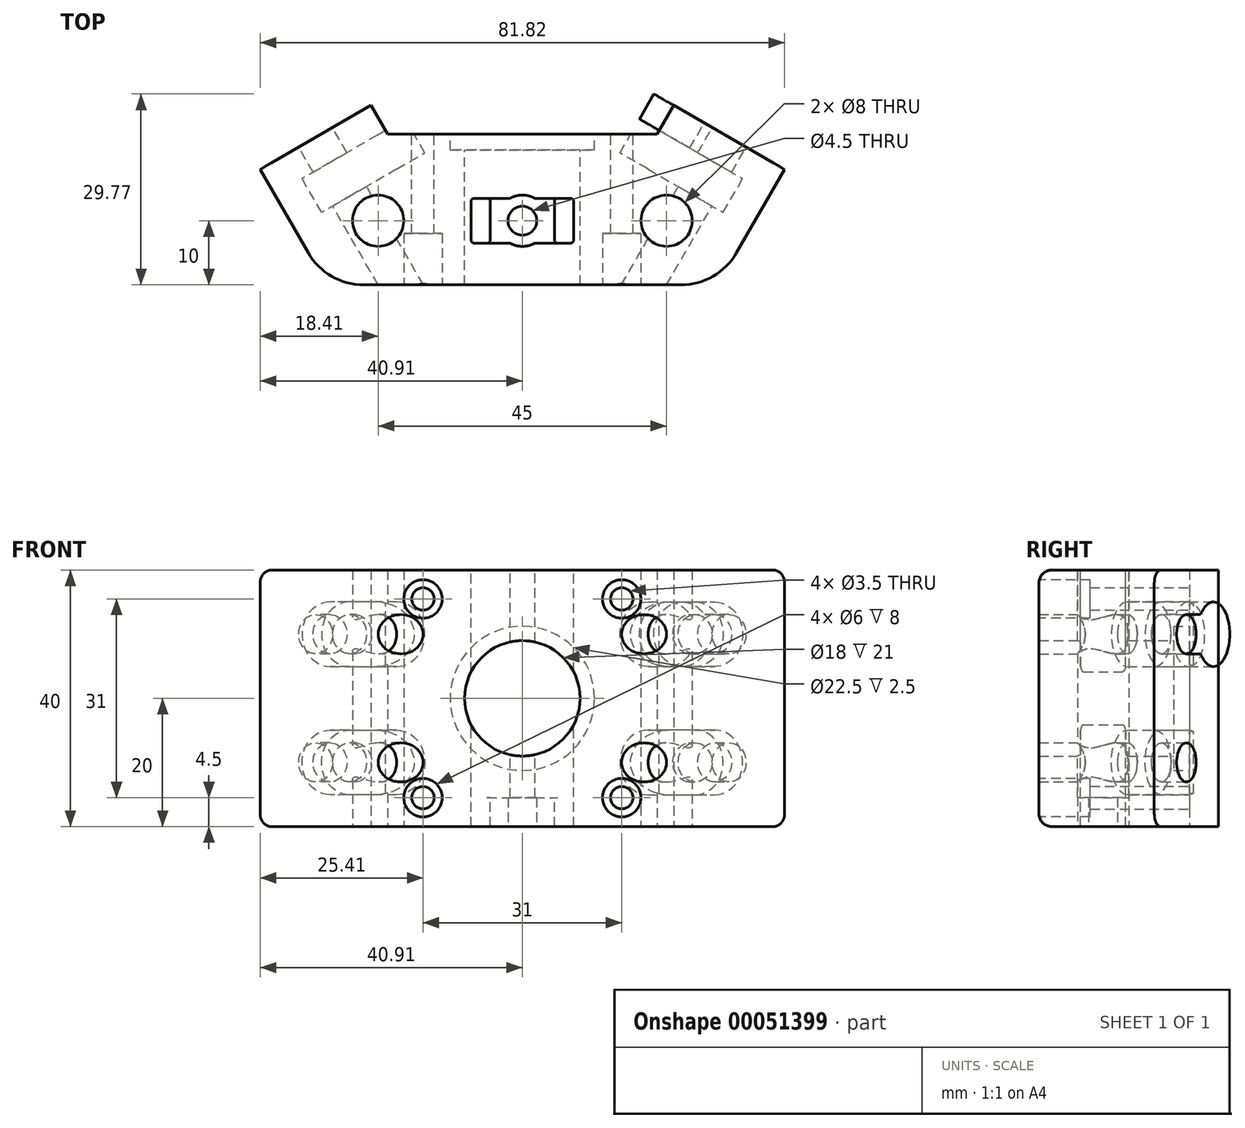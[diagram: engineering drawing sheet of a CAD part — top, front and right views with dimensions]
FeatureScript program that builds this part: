
annotation { "Feature Type Name" : "Feature", "Feature Type Description" : "" }
export const myFeature = defineFeature(function(context is Context, id is Id, definition is map)
    precondition{}
    {
        {
            var Q0;
            Q0=qCreatedBy(makeId("Top.planeOp"),FACE);
            var sketch = newSketch(context, id + "F0", { "sketchPlane" : qUnion([Q0])});
            skLineSegment(sketch, "E0", {"start": v(-22.5, 0) * mm, "end": v(22.5, 0) * mm, "construction": true});
            skCircle(sketch, "E1", {"center": v(22.5, 0) * mm, "radius": 4 * mm});
            skCircle(sketch, "E2", {"center": v(-22.5, 0) * mm, "radius": 4 * mm});
            skLineSegment(sketch, "E3", {"start": v(0, 0) * mm, "end": v(0, 13.5) * mm, "construction": true});
            skLineSegment(sketch, "E4", {"start": v(-21, 13.5) * mm, "end": v(21, 13.5) * mm});
            skLineSegment(sketch, "E5", {"start": v(23.6, 18) * mm, "end": v(40.91, 8) * mm});
            skLineSegment(sketch, "E6", {"start": v(40.91, 8) * mm, "end": v(33.41, -5) * mm});
            skLineSegment(sketch, "E7", {"start": v(24.75, -10) * mm, "end": v(-24.75, -10) * mm});
            skLineSegment(sketch, "E8", {"start": v(0, -10) * mm, "end": v(0, 0) * mm, "construction": true});
            skLineSegment(sketch, "E9", {"start": v(23.6, 18) * mm, "end": v(21, 13.5) * mm});
            skLineSegment(sketch, "E10", {"start": v(22.5, 0) * mm, "end": v(30.56, 13.97) * mm, "construction": true});
            skArc(sketch, "E11", {"start": v(33.41, -5) * mm, "mid": v(29.75, -8.66) * mm, "end": v(24.75, -10) * mm});
            skArc(sketch, "E12.MirrorCS", {"start": v(-33.41, -5) * mm, "mid": v(-29.75, -8.66) * mm, "end": v(-24.75, -10) * mm});
            skLineSegment(sketch, "E13.MirrorCS", {"start": v(-40.91, 8) * mm, "end": v(-33.41, -5) * mm});
            skLineSegment(sketch, "E14.MirrorCS", {"start": v(-23.6, 18) * mm, "end": v(-21, 13.5) * mm});
            skLineSegment(sketch, "E15.MirrorCS", {"start": v(-23.6, 18) * mm, "end": v(-40.91, 8) * mm});
            skSolve(sketch);
        }
        {
            var Q0;
            Q0 = qSketchRegion(id + "F0", true);
            extrude(context, id + "F1", {"entities" : qUnion([Q0]), "endBound" : BoundingType.SYMMETRIC, "depth" : 40 * mm});
        }
        {
            var Q0;
            Q0=makeQuery(id+"F1.opExtrude","SWEPT_FACE",FACE,{"disambiguationData":[OSD([sQuery(id+"F0.wireOp",EDGE,"E4")])]});
            var sketch = newSketch(context, id + "F2", { "sketchPlane" : qUnion([Q0])});
            skLineSegment(sketch, "E16", {"start": v(0, 20) * mm, "end": v(0, -20) * mm, "construction": true});
            skCircle(sketch, "E17", {"center": v(0, 0) * mm, "radius": 11.25 * mm});
            skSolve(sketch);
        }
        {
            var Q0;
            Q0 = qSketchRegion(id + "F2", true);
            extrude(context, id + "F3", {"entities" : qUnion([Q0]), "operationType" : NewBodyOperationType.REMOVE, "oppositeDirection" : true, "depth" : 2.5 * mm});
        }
        {
            var Q0;
            Q0=makeQuery(id+"F3.boolean.opBoolean","COPY",FACE,{"derivedFrom":makeQuery(id+"F3.opExtrude","CAP_FACE",FACE,{"disambiguationData":[OSD([sQuery(id+"F2.wireOp",EDGE,"E17")])],"isStart":false})});
            var sketch = newSketch(context, id + "F4", { "sketchPlane" : qUnion([Q0])});
            skCircle(sketch, "E18", {"center": v(0, 0) * mm, "radius": 9 * mm});
            skSolve(sketch);
        }
        {
            var Q0;
            Q0 = qSketchRegion(id + "F4", true);
            extrude(context, id + "F5", {"entities" : qUnion([Q0]), "operationType" : NewBodyOperationType.REMOVE, "endBound" : BoundingType.UP_TO_NEXT, "oppositeDirection" : true, "depth" : 25 * mm});
        }
        {
            var Q0;
            Q0=makeQuery(id+"F1.opExtrude","SWEPT_FACE",FACE,{"disambiguationData":[OSD([sQuery(id+"F0.wireOp",EDGE,"E4")])]});
            var sketch = newSketch(context, id + "F6", { "sketchPlane" : qUnion([Q0])});
            skLineSegment(sketch, "E19.rect.bottom", {"start": v(15.5, 15.5) * mm, "end": v(-15.5, 15.5) * mm, "construction": true});
            skLineSegment(sketch, "E19.rect.top", {"start": v(15.5, -15.5) * mm, "end": v(-15.5, -15.5) * mm, "construction": true});
            skLineSegment(sketch, "E19.rect.left", {"start": v(15.5, 15.5) * mm, "end": v(15.5, -15.5) * mm, "construction": true});
            skLineSegment(sketch, "E19.rect.right", {"start": v(-15.5, 15.5) * mm, "end": v(-15.5, -15.5) * mm, "construction": true});
            skPoint(sketch, "E19.rect.middle", {"position": v(0, 0) * mm});
            skSolve(sketch);
        }
        {
            var Q0;
            Q0=sQuery(id+"F6.wireOp",VERTEX,"E19.rect.right.start");
            var Q1;
            Q1=sQuery(id+"F6.wireOp",VERTEX,"E19.rect.left.start");
            var Q2;
            Q2=sQuery(id+"F6.wireOp",VERTEX,"E19.rect.left.end");
            var Q3;
            Q3=sQuery(id+"F6.wireOp",VERTEX,"E19.rect.right.end");
            var Q4;
            Q4=makeQuery(id+"F1.opExtrude","SWEPT_BODY",BODY,{"disambiguationData":[OSD([sQuery(id+"F0.wireOp",EDGE,"E1"),sQuery(id+"F0.wireOp",EDGE,"E2"),sQuery(id+"F0.wireOp",EDGE,"E4"),sQuery(id+"F0.wireOp",EDGE,"E5"),sQuery(id+"F0.wireOp",EDGE,"E6"),sQuery(id+"F0.wireOp",EDGE,"E7"),sQuery(id+"F0.wireOp",EDGE,"E9"),sQuery(id+"F0.wireOp",EDGE,"E11"),sQuery(id+"F0.wireOp",EDGE,"E12.MirrorCS"),sQuery(id+"F0.wireOp",EDGE,"E13.MirrorCS"),sQuery(id+"F0.wireOp",EDGE,"E14.MirrorCS"),sQuery(id+"F0.wireOp",EDGE,"E15.MirrorCS")])]});
            hole(context, id + "F7", {"style" : HoleStyle.SIMPLE, "holeDiameter" : 3.5 * mm, "endStyle" : HoleEndStyle.THROUGH, "locations" : qUnion([Q0, Q1, Q2, Q3]), "scope" : qUnion([Q4])});
        }
        {
            var Q0;
            Q0=makeQuery(id+"F1.opExtrude","SWEPT_FACE",FACE,{"disambiguationData":[OSD([sQuery(id+"F0.wireOp",EDGE,"E5")])]});
            var sketch = newSketch(context, id + "F8", { "sketchPlane" : qUnion([Q0])});
            skLineSegment(sketch, "E20", {"start": v(-21.44, 20) * mm, "end": v(-21.44, 10) * mm, "construction": true});
            skLineSegment(sketch, "E21", {"start": v(-21.44, 10) * mm, "end": v(-21.44, -10) * mm, "construction": true});
            skLineSegment(sketch, "E22", {"start": v(-21.44, -10) * mm, "end": v(-21.44, -20) * mm, "construction": true});
            skSolve(sketch);
        }
        {
            var Q0;
            Q0=makeQuery(id+"F1.opExtrude","SWEPT_FACE",FACE,{"disambiguationData":[OSD([sQuery(id+"F0.wireOp",EDGE,"E15.MirrorCS")])]});
            var sketch = newSketch(context, id + "F9", { "sketchPlane" : qUnion([Q0])});
            skLineSegment(sketch, "E23", {"start": v(21.44, 20) * mm, "end": v(21.44, 10) * mm, "construction": true});
            skLineSegment(sketch, "E24", {"start": v(21.44, 10) * mm, "end": v(21.44, -10) * mm, "construction": true});
            skLineSegment(sketch, "E25", {"start": v(21.44, -10) * mm, "end": v(21.44, -20) * mm, "construction": true});
            skSolve(sketch);
        }
        {
            var Q0;
            Q0=sQuery(id+"F8.wireOp",VERTEX,"E20.end");
            var Q1;
            Q1=sQuery(id+"F8.wireOp",VERTEX,"E21.end");
            var Q2;
            Q2=sQuery(id+"F9.wireOp",VERTEX,"E23.end");
            var Q3;
            Q3=sQuery(id+"F9.wireOp",VERTEX,"E24.end");
            var Q4;
            Q4=makeQuery(id+"F1.opExtrude","SWEPT_BODY",BODY,{"disambiguationData":[OSD([sQuery(id+"F0.wireOp",EDGE,"E1"),sQuery(id+"F0.wireOp",EDGE,"E2"),sQuery(id+"F0.wireOp",EDGE,"E4"),sQuery(id+"F0.wireOp",EDGE,"E5"),sQuery(id+"F0.wireOp",EDGE,"E6"),sQuery(id+"F0.wireOp",EDGE,"E7"),sQuery(id+"F0.wireOp",EDGE,"E9"),sQuery(id+"F0.wireOp",EDGE,"E11"),sQuery(id+"F0.wireOp",EDGE,"E12.MirrorCS"),sQuery(id+"F0.wireOp",EDGE,"E13.MirrorCS"),sQuery(id+"F0.wireOp",EDGE,"E14.MirrorCS"),sQuery(id+"F0.wireOp",EDGE,"E15.MirrorCS")])]});
            hole(context, id + "F10", {"style" : HoleStyle.SIMPLE, "holeDiameter" : 6.1 * mm, "endStyle" : HoleEndStyle.THROUGH, "locations" : qUnion([Q0, Q1, Q2, Q3]), "scope" : qUnion([Q4])});
        }
        {
            var Q0;
            Q0=makeQuery(id+"F1.opExtrude","CAP_FACE",FACE,{"disambiguationData":[OSD([sQuery(id+"F0.wireOp",EDGE,"E1"),sQuery(id+"F0.wireOp",EDGE,"E2"),sQuery(id+"F0.wireOp",EDGE,"E4"),sQuery(id+"F0.wireOp",EDGE,"E5"),sQuery(id+"F0.wireOp",EDGE,"E6"),sQuery(id+"F0.wireOp",EDGE,"E7"),sQuery(id+"F0.wireOp",EDGE,"E9"),sQuery(id+"F0.wireOp",EDGE,"E11"),sQuery(id+"F0.wireOp",EDGE,"E12.MirrorCS"),sQuery(id+"F0.wireOp",EDGE,"E13.MirrorCS"),sQuery(id+"F0.wireOp",EDGE,"E14.MirrorCS"),sQuery(id+"F0.wireOp",EDGE,"E15.MirrorCS")])],"isStart":true});
            var sketch = newSketch(context, id + "F11", { "sketchPlane" : qUnion([Q0])});
            skLineSegment(sketch, "E26", {"start": v(0, 10) * mm, "end": v(0, 0) * mm, "construction": true});
            skPoint(sketch, "E26.endSnap0", {"position": v(0, 10) * mm});
            skSolve(sketch);
        }
        {
            var Q0;
            Q0=sQuery(id+"F11.wireOp",VERTEX,"E26.end");
            var Q1;
            Q1=makeQuery(id+"F1.opExtrude","SWEPT_BODY",BODY,{"disambiguationData":[OSD([sQuery(id+"F0.wireOp",EDGE,"E1"),sQuery(id+"F0.wireOp",EDGE,"E2"),sQuery(id+"F0.wireOp",EDGE,"E4"),sQuery(id+"F0.wireOp",EDGE,"E5"),sQuery(id+"F0.wireOp",EDGE,"E6"),sQuery(id+"F0.wireOp",EDGE,"E7"),sQuery(id+"F0.wireOp",EDGE,"E9"),sQuery(id+"F0.wireOp",EDGE,"E11"),sQuery(id+"F0.wireOp",EDGE,"E12.MirrorCS"),sQuery(id+"F0.wireOp",EDGE,"E13.MirrorCS"),sQuery(id+"F0.wireOp",EDGE,"E14.MirrorCS"),sQuery(id+"F0.wireOp",EDGE,"E15.MirrorCS")])]});
            hole(context, id + "F12", {"style" : HoleStyle.SIMPLE, "holeDiameter" : 4.5 * mm, "endStyle" : HoleEndStyle.THROUGH, "locations" : qUnion([Q0]), "scope" : qUnion([Q1])});
        }
        {
            var Q0;
            Q0=makeQuery(id+"F1.opExtrude","SWEPT_FACE",FACE,{"disambiguationData":[OSD([sQuery(id+"F0.wireOp",EDGE,"E5")])]});
            cPlane(context, id + "F13", {"entities" : qUnion([Q0]), "cplaneType" : CPlaneType.OFFSET, "offset" : 4.5 * mm, "oppositeDirection" : true, "width" : 150 * mm, "height" : 150 * mm});
        }
        {
            var Q0;
            Q0=qCreatedBy(id+"F13.planeOp",FACE);
            var sketch = newSketch(context, id + "F14", { "sketchPlane" : qUnion([Q0])});
            skLineSegment(sketch, "E27", {"start": v(-21.44, 10) * mm, "end": v(-12.94, 10) * mm, "construction": true});
            skLineSegment(sketch, "E28", {"start": v(-21.44, 13.05) * mm, "end": v(-17.41, 13.05) * mm, "construction": true});
            skLineSegment(sketch, "E29", {"start": v(-12.94, 15.05) * mm, "end": v(-21.44, 15.05) * mm});
            skLineSegment(sketch, "E30", {"start": v(-21.44, 4.95) * mm, "end": v(-21.44, 4.95) * mm});
            skArc(sketch, "E31", {"start": v(-12.94, 15.05) * mm, "mid": v(-17.99, 10) * mm, "end": v(-12.94, 4.95) * mm, "construction": true});
            skArc(sketch, "E32", {"start": v(-12.94, 4.95) * mm, "mid": v(-7.89, 10) * mm, "end": v(-12.94, 15.05) * mm});
            skLineSegment(sketch, "E33", {"start": v(-21.44, 15.05) * mm, "end": v(-21.44, 15.05) * mm});
            skLineSegment(sketch, "E34", {"start": v(-21.44, 4.95) * mm, "end": v(-12.94, 4.95) * mm});
            skArc(sketch, "E35", {"start": v(-21.44, 15.05) * mm, "mid": v(-26.49, 10) * mm, "end": v(-21.44, 4.95) * mm});
            skArc(sketch, "E36", {"start": v(-21.44, 4.95) * mm, "mid": v(-16.39, 10) * mm, "end": v(-21.44, 15.05) * mm, "construction": true});
            skSolve(sketch);
        }
        {
            var Q0;
            Q0 = qSketchRegion(id + "F14", true);
            extrude(context, id + "F15", {"entities" : qUnion([Q0]), "oppositeDirection" : true, "depth" : 6.1 * mm});
        }
        {
            var Q0;
            Q0=makeQuery(id+"F1.opExtrude","SWEPT_FACE",FACE,{"disambiguationData":[OSD([sQuery(id+"F0.wireOp",EDGE,"E5")])]});
            var sketch = newSketch(context, id + "F16", { "sketchPlane" : qUnion([Q0])});
            skLineSegment(sketch, "E37.0", {"start": v(-21.44, 13.05) * mm, "end": v(-21.44, 13.05) * mm});
            skLineSegment(sketch, "E38", {"start": v(-21.44, 13.05) * mm, "end": v(-16.96, 13.05) * mm});
            skArc(sketch, "E39.0", {"start": v(-21.44, 13.05) * mm, "mid": v(-24.49, 10) * mm, "end": v(-21.44, 6.95) * mm});
            skArc(sketch, "E40", {"start": v(-16.96, 6.95) * mm, "mid": v(-7.89, 10) * mm, "end": v(-16.96, 13.05) * mm});
            skLineSegment(sketch, "E41", {"start": v(-21.44, 6.95) * mm, "end": v(-16.96, 6.95) * mm});
            skSolve(sketch);
        }
        {
            var Q0;
            Q0 = qSketchRegion(id + "F16", true);
            var Q1;
            Q1=makeQuery(id+"F15.boolean.opBoolean","COPY",FACE,{"derivedFrom":makeQuery(id+"F15.opExtrude","CAP_FACE",FACE,{"disambiguationData":[OSD([sQuery(id+"F14.wireOp",EDGE,"E29"),sQuery(id+"F14.wireOp",EDGE,"E32"),sQuery(id+"F14.wireOp",EDGE,"E34"),sQuery(id+"F14.wireOp",EDGE,"E35")])],"isStart":false})});
            var Q2;
            Q2=makeQuery(id+"F15.opExtrude","SWEPT_BODY",BODY,{"disambiguationData":[OSD([sQuery(id+"F14.wireOp",EDGE,"E29"),sQuery(id+"F14.wireOp",EDGE,"E32"),sQuery(id+"F14.wireOp",EDGE,"E34"),sQuery(id+"F14.wireOp",EDGE,"E35")])]});
            extrude(context, id + "F17", {"entities" : qUnion([Q0]), "endBound" : BoundingType.UP_TO_BODY, "oppositeDirection" : true, "endBoundEntityFace" : qUnion([Q1]), "endBoundEntityBody" : qUnion([Q2]), "depth" : 25 * mm});
        }
        {
            var Q0;
            Q0=makeQuery(id+"F15.opExtrude","SWEPT_BODY",BODY,{"disambiguationData":[OSD([sQuery(id+"F14.wireOp",EDGE,"E29"),sQuery(id+"F14.wireOp",EDGE,"E32"),sQuery(id+"F14.wireOp",EDGE,"E34"),sQuery(id+"F14.wireOp",EDGE,"E35")])]});
            var Q1;
            Q1=qCreatedBy(makeId("Top.planeOp"),FACE);
            mirror(context, id + "F18", {"entities" : qUnion([Q0]), "mirrorPlane" : qUnion([Q1])});
        }
        {
            var Q0;
            Q0=makeQuery(id+"F15.opExtrude","SWEPT_BODY",BODY,{"disambiguationData":[OSD([sQuery(id+"F14.wireOp",EDGE,"E29"),sQuery(id+"F14.wireOp",EDGE,"E32"),sQuery(id+"F14.wireOp",EDGE,"E34"),sQuery(id+"F14.wireOp",EDGE,"E35")])]});
            var Q1;
            Q1=makeQuery(id+"F18.opPattern","COPY",BODY,{"derivedFrom":makeQuery(id+"F15.opExtrude","SWEPT_BODY",BODY,{"disambiguationData":[OSD([sQuery(id+"F14.wireOp",EDGE,"E29"),sQuery(id+"F14.wireOp",EDGE,"E32"),sQuery(id+"F14.wireOp",EDGE,"E34"),sQuery(id+"F14.wireOp",EDGE,"E35")])]}),"instanceName":"1"});
            var Q2;
            Q2=qCreatedBy(makeId("Right.planeOp"),FACE);
            mirror(context, id + "F19", {"entities" : qUnion([Q0, Q1]), "mirrorPlane" : qUnion([Q2])});
        }
        {
            var Q0;
            Q0=makeQuery(id+"F18.opPattern","COPY",BODY,{"derivedFrom":makeQuery(id+"F15.opExtrude","SWEPT_BODY",BODY,{"disambiguationData":[OSD([sQuery(id+"F14.wireOp",EDGE,"E29"),sQuery(id+"F14.wireOp",EDGE,"E32"),sQuery(id+"F14.wireOp",EDGE,"E34"),sQuery(id+"F14.wireOp",EDGE,"E35")])]}),"instanceName":"1"});
            var Q1;
            Q1=makeQuery(id+"F19.opPattern","COPY",BODY,{"derivedFrom":makeQuery(id+"F15.opExtrude","SWEPT_BODY",BODY,{"disambiguationData":[OSD([sQuery(id+"F14.wireOp",EDGE,"E29"),sQuery(id+"F14.wireOp",EDGE,"E32"),sQuery(id+"F14.wireOp",EDGE,"E34"),sQuery(id+"F14.wireOp",EDGE,"E35")])]}),"instanceName":"1"});
            var Q2;
            Q2=makeQuery(id+"F19.opPattern","COPY",BODY,{"derivedFrom":makeQuery(id+"F18.opPattern","COPY",BODY,{"derivedFrom":makeQuery(id+"F15.opExtrude","SWEPT_BODY",BODY,{"disambiguationData":[OSD([sQuery(id+"F14.wireOp",EDGE,"E29"),sQuery(id+"F14.wireOp",EDGE,"E32"),sQuery(id+"F14.wireOp",EDGE,"E34"),sQuery(id+"F14.wireOp",EDGE,"E35")])]}),"instanceName":"1"}),"instanceName":"1"});
            var Q3;
            Q3=makeQuery(id+"F15.opExtrude","SWEPT_BODY",BODY,{"disambiguationData":[OSD([sQuery(id+"F14.wireOp",EDGE,"E29"),sQuery(id+"F14.wireOp",EDGE,"E32"),sQuery(id+"F14.wireOp",EDGE,"E34"),sQuery(id+"F14.wireOp",EDGE,"E35")])]});
            var Q4;
            Q4=makeQuery(id+"F1.opExtrude","SWEPT_BODY",BODY,{"disambiguationData":[OSD([sQuery(id+"F0.wireOp",EDGE,"E1"),sQuery(id+"F0.wireOp",EDGE,"E2"),sQuery(id+"F0.wireOp",EDGE,"E4"),sQuery(id+"F0.wireOp",EDGE,"E5"),sQuery(id+"F0.wireOp",EDGE,"E6"),sQuery(id+"F0.wireOp",EDGE,"E7"),sQuery(id+"F0.wireOp",EDGE,"E9"),sQuery(id+"F0.wireOp",EDGE,"E11"),sQuery(id+"F0.wireOp",EDGE,"E12.MirrorCS"),sQuery(id+"F0.wireOp",EDGE,"E13.MirrorCS"),sQuery(id+"F0.wireOp",EDGE,"E14.MirrorCS"),sQuery(id+"F0.wireOp",EDGE,"E15.MirrorCS")])]});
            booleanBodies(context, id + "F20", {"operationType" : BooleanOperationType.SUBTRACTION, "tools" : qUnion([Q0, Q1, Q2, Q3]), "targets" : qUnion([Q4])});
        }
        {
            var Q0;
            Q0=makeQuery(id+"F1.opExtrude","CAP_FACE",FACE,{"disambiguationData":[OSD([sQuery(id+"F0.wireOp",EDGE,"E1"),sQuery(id+"F0.wireOp",EDGE,"E2"),sQuery(id+"F0.wireOp",EDGE,"E4"),sQuery(id+"F0.wireOp",EDGE,"E5"),sQuery(id+"F0.wireOp",EDGE,"E6"),sQuery(id+"F0.wireOp",EDGE,"E7"),sQuery(id+"F0.wireOp",EDGE,"E9"),sQuery(id+"F0.wireOp",EDGE,"E11"),sQuery(id+"F0.wireOp",EDGE,"E12.MirrorCS"),sQuery(id+"F0.wireOp",EDGE,"E13.MirrorCS"),sQuery(id+"F0.wireOp",EDGE,"E14.MirrorCS"),sQuery(id+"F0.wireOp",EDGE,"E15.MirrorCS")])],"isStart":false});
            var sketch = newSketch(context, id + "F21", { "sketchPlane" : qUnion([Q0])});
            skCircle(sketch, "E42", {"center": v(0, 0) * mm, "radius": 4 * mm});
            skSolve(sketch);
        }
        {
            var Q0;
            Q0 = qSketchRegion(id + "F21", true);
            var Q1;
            Q1=sQuery(id+"F21.wireOp",EDGE,"E42");
            extrude(context, id + "F22", {"entities" : qUnion([Q0]), "operationType" : NewBodyOperationType.REMOVE, "surfaceEntities" : qUnion([Q1]), "oppositeDirection" : true, "depth" : (40 - 4.5) * mm});
        }
        {
            var Q0;
            Q0=makeQuery(id+"F1.opExtrude","SWEPT_FACE",FACE,{"disambiguationData":[OSD([sQuery(id+"F0.wireOp",EDGE,"E7")])]});
            var sketch = newSketch(context, id + "F23", { "sketchPlane" : qUnion([Q0])});
            skCircle(sketch, "E43", {"center": v(-15.5, 15.5) * mm, "radius": 3 * mm});
            skCircle(sketch, "E44", {"center": v(15.5, 15.5) * mm, "radius": 3 * mm});
            skCircle(sketch, "E45", {"center": v(15.5, -15.5) * mm, "radius": 3 * mm});
            skCircle(sketch, "E46", {"center": v(-15.5, -15.5) * mm, "radius": 3 * mm});
            skSolve(sketch);
        }
        {
            var Q0;
            Q0 = qSketchRegion(id + "F23", true);
            extrude(context, id + "F24", {"entities" : qUnion([Q0]), "operationType" : NewBodyOperationType.REMOVE, "oppositeDirection" : true, "depth" : 8 * mm});
        }
        {
            var Q0;
            Q0=makeQuery(id+"F1.opExtrude","CAP_FACE",FACE,{"disambiguationData":[OSD([sQuery(id+"F0.wireOp",EDGE,"E1"),sQuery(id+"F0.wireOp",EDGE,"E2"),sQuery(id+"F0.wireOp",EDGE,"E4"),sQuery(id+"F0.wireOp",EDGE,"E5"),sQuery(id+"F0.wireOp",EDGE,"E6"),sQuery(id+"F0.wireOp",EDGE,"E7"),sQuery(id+"F0.wireOp",EDGE,"E9"),sQuery(id+"F0.wireOp",EDGE,"E11"),sQuery(id+"F0.wireOp",EDGE,"E12.MirrorCS"),sQuery(id+"F0.wireOp",EDGE,"E13.MirrorCS"),sQuery(id+"F0.wireOp",EDGE,"E14.MirrorCS"),sQuery(id+"F0.wireOp",EDGE,"E15.MirrorCS")])],"isStart":false});
            var sketch = newSketch(context, id + "F25", { "sketchPlane" : qUnion([Q0])});
            skLineSegment(sketch, "E47.rect.bottom", {"start": v(8, 3.5) * mm, "end": v(-8, 3.5) * mm});
            skLineSegment(sketch, "E47.rect.top", {"start": v(8, -3.5) * mm, "end": v(-8, -3.5) * mm});
            skLineSegment(sketch, "E47.rect.left", {"start": v(8, 3.5) * mm, "end": v(8, -3.5) * mm});
            skLineSegment(sketch, "E47.rect.right", {"start": v(-8, 3.5) * mm, "end": v(-8, -3.5) * mm});
            skPoint(sketch, "E47.rect.middle", {"position": v(0, 0) * mm});
            skSolve(sketch);
        }
        {
            var Q0;
            Q0 = qSketchRegion(id + "F25", true);
            var Q1;
            Q1=makeQuery(id+"F22.boolean.opBoolean","COPY",FACE,{"derivedFrom":makeQuery(id+"F22.opExtrude","CAP_FACE",FACE,{"disambiguationData":[OSD([sQuery(id+"F21.wireOp",EDGE,"E42")])],"isStart":false})});
            extrude(context, id + "F26", {"entities" : qUnion([Q0]), "operationType" : NewBodyOperationType.REMOVE, "endBound" : BoundingType.UP_TO_SURFACE, "oppositeDirection" : true, "endBoundEntityFace" : qUnion([Q1]), "depth" : 25 * mm});
        }
        {
            var Q0;
            {var subQ0=sQuery(id+"F21.wireOp",EDGE,"E42");Q0=makeQuery(id+"F26.boolean.opBoolean","MERGE",FACE,{"derivedFrom":[makeQuery(id+"F22.boolean.opBoolean","COPY",FACE,{"derivedFrom":makeQuery(id+"F22.opExtrude","CAP_FACE",FACE,{"disambiguationData":[OSD([subQ0])],"isStart":false})}),makeQuery(id+"F26.opExtrude","CAP_FACE",FACE,{"disambiguationData":[OSD([subQ0])],"isStart":false})]});}
            var sketch = newSketch(context, id + "F27", { "sketchPlane" : qUnion([Q0])});
            skLineSegment(sketch, "E48.bottom", {"start": v(-8, 3.5) * mm, "end": v(-5, 3.5) * mm});
            skLineSegment(sketch, "E48.top", {"start": v(-8, -3.5) * mm, "end": v(-5, -3.5) * mm});
            skLineSegment(sketch, "E48.left", {"start": v(-8, 3.5) * mm, "end": v(-8, -3.5) * mm});
            skLineSegment(sketch, "E48.right", {"start": v(-5, 3.5) * mm, "end": v(-5, -3.5) * mm});
            skLineSegment(sketch, "E49.bottom", {"start": v(8, 3.5) * mm, "end": v(5, 3.5) * mm});
            skLineSegment(sketch, "E49.top", {"start": v(8, -3.5) * mm, "end": v(5, -3.5) * mm});
            skLineSegment(sketch, "E49.left", {"start": v(8, 3.5) * mm, "end": v(8, -3.5) * mm});
            skLineSegment(sketch, "E49.right", {"start": v(5, 3.5) * mm, "end": v(5, -3.5) * mm});
            skSolve(sketch);
        }
        {
            var Q0;
            Q0 = qSketchRegion(id + "F27", true);
            extrude(context, id + "F28", {"entities" : qUnion([Q0]), "operationType" : NewBodyOperationType.REMOVE, "endBound" : BoundingType.THROUGH_ALL, "oppositeDirection" : true, "depth" : 25 * mm});
        }
        {
            var Q0;
            {var subQ0=sQuery(id+"F25.wireOp",EDGE,"E47.rect.bottom");var subQ1=sQuery(id+"F25.wireOp",EDGE,"E47.rect.right");Q0=makeQuery(id+"F26.boolean.opBoolean","COPY",EDGE,{"disambiguationData":[TD([makeQuery(id+"F1.opExtrude","CAP_FACE",FACE,{"disambiguationData":[OSD([sQuery(id+"F0.wireOp",EDGE,"E1"),sQuery(id+"F0.wireOp",EDGE,"E2"),sQuery(id+"F0.wireOp",EDGE,"E4"),sQuery(id+"F0.wireOp",EDGE,"E5"),sQuery(id+"F0.wireOp",EDGE,"E6"),sQuery(id+"F0.wireOp",EDGE,"E7"),sQuery(id+"F0.wireOp",EDGE,"E9"),sQuery(id+"F0.wireOp",EDGE,"E11"),sQuery(id+"F0.wireOp",EDGE,"E12.MirrorCS"),sQuery(id+"F0.wireOp",EDGE,"E13.MirrorCS"),sQuery(id+"F0.wireOp",EDGE,"E14.MirrorCS"),sQuery(id+"F0.wireOp",EDGE,"E15.MirrorCS")])],"isStart":false})])],"derivedFrom":makeQuery(id+"F26.opExtrude","SWEPT_EDGE",EDGE,{"disambiguationData":[OSD([subQ0,subQ1])]})});}
            var Q1;
            {var subQ0=sQuery(id+"F25.wireOp",EDGE,"E47.rect.top");var subQ1=sQuery(id+"F25.wireOp",EDGE,"E47.rect.right");Q1=makeQuery(id+"F26.boolean.opBoolean","COPY",EDGE,{"disambiguationData":[TD([makeQuery(id+"F1.opExtrude","CAP_FACE",FACE,{"disambiguationData":[OSD([sQuery(id+"F0.wireOp",EDGE,"E1"),sQuery(id+"F0.wireOp",EDGE,"E2"),sQuery(id+"F0.wireOp",EDGE,"E4"),sQuery(id+"F0.wireOp",EDGE,"E5"),sQuery(id+"F0.wireOp",EDGE,"E6"),sQuery(id+"F0.wireOp",EDGE,"E7"),sQuery(id+"F0.wireOp",EDGE,"E9"),sQuery(id+"F0.wireOp",EDGE,"E11"),sQuery(id+"F0.wireOp",EDGE,"E12.MirrorCS"),sQuery(id+"F0.wireOp",EDGE,"E13.MirrorCS"),sQuery(id+"F0.wireOp",EDGE,"E14.MirrorCS"),sQuery(id+"F0.wireOp",EDGE,"E15.MirrorCS")])],"isStart":false})])],"derivedFrom":makeQuery(id+"F26.opExtrude","SWEPT_EDGE",EDGE,{"disambiguationData":[OSD([subQ0,subQ1])]})});}
            var Q2;
            {var subQ0=sQuery(id+"F25.wireOp",EDGE,"E47.rect.top");var subQ1=sQuery(id+"F25.wireOp",EDGE,"E47.rect.left");Q2=makeQuery(id+"F26.boolean.opBoolean","COPY",EDGE,{"disambiguationData":[TD([makeQuery(id+"F1.opExtrude","CAP_FACE",FACE,{"disambiguationData":[OSD([sQuery(id+"F0.wireOp",EDGE,"E1"),sQuery(id+"F0.wireOp",EDGE,"E2"),sQuery(id+"F0.wireOp",EDGE,"E4"),sQuery(id+"F0.wireOp",EDGE,"E5"),sQuery(id+"F0.wireOp",EDGE,"E6"),sQuery(id+"F0.wireOp",EDGE,"E7"),sQuery(id+"F0.wireOp",EDGE,"E9"),sQuery(id+"F0.wireOp",EDGE,"E11"),sQuery(id+"F0.wireOp",EDGE,"E12.MirrorCS"),sQuery(id+"F0.wireOp",EDGE,"E13.MirrorCS"),sQuery(id+"F0.wireOp",EDGE,"E14.MirrorCS"),sQuery(id+"F0.wireOp",EDGE,"E15.MirrorCS")])],"isStart":false})])],"derivedFrom":makeQuery(id+"F26.opExtrude","SWEPT_EDGE",EDGE,{"disambiguationData":[OSD([subQ0,subQ1])]})});}
            var Q3;
            {var subQ0=sQuery(id+"F25.wireOp",EDGE,"E47.rect.bottom");var subQ1=sQuery(id+"F25.wireOp",EDGE,"E47.rect.left");Q3=makeQuery(id+"F26.boolean.opBoolean","COPY",EDGE,{"disambiguationData":[TD([makeQuery(id+"F1.opExtrude","CAP_FACE",FACE,{"disambiguationData":[OSD([sQuery(id+"F0.wireOp",EDGE,"E1"),sQuery(id+"F0.wireOp",EDGE,"E2"),sQuery(id+"F0.wireOp",EDGE,"E4"),sQuery(id+"F0.wireOp",EDGE,"E5"),sQuery(id+"F0.wireOp",EDGE,"E6"),sQuery(id+"F0.wireOp",EDGE,"E7"),sQuery(id+"F0.wireOp",EDGE,"E9"),sQuery(id+"F0.wireOp",EDGE,"E11"),sQuery(id+"F0.wireOp",EDGE,"E12.MirrorCS"),sQuery(id+"F0.wireOp",EDGE,"E13.MirrorCS"),sQuery(id+"F0.wireOp",EDGE,"E14.MirrorCS"),sQuery(id+"F0.wireOp",EDGE,"E15.MirrorCS")])],"isStart":false})])],"derivedFrom":makeQuery(id+"F26.opExtrude","SWEPT_EDGE",EDGE,{"disambiguationData":[OSD([subQ0,subQ1])]})});}
            var Q4;
            {var subQ0=sQuery(id+"F25.wireOp",EDGE,"E47.rect.bottom");var subQ1=sQuery(id+"F21.wireOp",EDGE,"E42");var subQ2=sQuery(id+"F25.wireOp",EDGE,"E47.rect.left");Q4=makeQuery(id+"F28.boolean.opBoolean","MERGE",EDGE,{"derivedFrom":[makeQuery(id+"F26.boolean.opBoolean","COPY",EDGE,{"disambiguationData":[TD([makeQuery(id+"F22.boolean.opBoolean","COPY",FACE,{"derivedFrom":makeQuery(id+"F22.opExtrude","CAP_FACE",FACE,{"disambiguationData":[OSD([subQ1])],"isStart":false})})])],"derivedFrom":makeQuery(id+"F26.opExtrude","SWEPT_EDGE",EDGE,{"disambiguationData":[OSD([subQ0,subQ2])]})}),makeQuery(id+"F28.opExtrude","SWEPT_EDGE",EDGE,{"disambiguationData":[OSD([sQuery(id+"F27.wireOp",EDGE,"E49.bottom"),sQuery(id+"F27.wireOp",EDGE,"E49.left")])]})]});}
            var Q5;
            Q5=makeQuery(id+"F28.boolean.opBoolean","COPY",EDGE,{"derivedFrom":makeQuery(id+"F28.opExtrude","SWEPT_EDGE",EDGE,{"disambiguationData":[OSD([sQuery(id+"F25.wireOp",EDGE,"E47.rect.bottom"),sQuery(id+"F27.wireOp",EDGE,"E49.bottom"),sQuery(id+"F27.wireOp",EDGE,"E49.right")])]})});
            var Q6;
            Q6=makeQuery(id+"F28.boolean.opBoolean","COPY",EDGE,{"derivedFrom":makeQuery(id+"F28.opExtrude","SWEPT_EDGE",EDGE,{"disambiguationData":[OSD([sQuery(id+"F25.wireOp",EDGE,"E47.rect.top"),sQuery(id+"F27.wireOp",EDGE,"E49.top"),sQuery(id+"F27.wireOp",EDGE,"E49.right")])]})});
            var Q7;
            {var subQ0=sQuery(id+"F25.wireOp",EDGE,"E47.rect.top");var subQ1=sQuery(id+"F21.wireOp",EDGE,"E42");var subQ2=sQuery(id+"F25.wireOp",EDGE,"E47.rect.left");Q7=makeQuery(id+"F28.boolean.opBoolean","MERGE",EDGE,{"derivedFrom":[makeQuery(id+"F26.boolean.opBoolean","COPY",EDGE,{"disambiguationData":[TD([makeQuery(id+"F22.boolean.opBoolean","COPY",FACE,{"derivedFrom":makeQuery(id+"F22.opExtrude","CAP_FACE",FACE,{"disambiguationData":[OSD([subQ1])],"isStart":false})})])],"derivedFrom":makeQuery(id+"F26.opExtrude","SWEPT_EDGE",EDGE,{"disambiguationData":[OSD([subQ0,subQ2])]})}),makeQuery(id+"F28.opExtrude","SWEPT_EDGE",EDGE,{"disambiguationData":[OSD([sQuery(id+"F27.wireOp",EDGE,"E49.top"),sQuery(id+"F27.wireOp",EDGE,"E49.left")])]})]});}
            var Q8;
            {var subQ0=sQuery(id+"F25.wireOp",EDGE,"E47.rect.bottom");var subQ1=sQuery(id+"F21.wireOp",EDGE,"E42");var subQ2=sQuery(id+"F25.wireOp",EDGE,"E47.rect.right");Q8=makeQuery(id+"F28.boolean.opBoolean","MERGE",EDGE,{"derivedFrom":[makeQuery(id+"F26.boolean.opBoolean","COPY",EDGE,{"disambiguationData":[TD([makeQuery(id+"F22.boolean.opBoolean","COPY",FACE,{"derivedFrom":makeQuery(id+"F22.opExtrude","CAP_FACE",FACE,{"disambiguationData":[OSD([subQ1])],"isStart":false})})])],"derivedFrom":makeQuery(id+"F26.opExtrude","SWEPT_EDGE",EDGE,{"disambiguationData":[OSD([subQ0,subQ2])]})}),makeQuery(id+"F28.opExtrude","SWEPT_EDGE",EDGE,{"disambiguationData":[OSD([sQuery(id+"F27.wireOp",EDGE,"E48.bottom"),sQuery(id+"F27.wireOp",EDGE,"E48.left")])]})]});}
            var Q9;
            {var subQ0=sQuery(id+"F25.wireOp",EDGE,"E47.rect.top");var subQ1=sQuery(id+"F21.wireOp",EDGE,"E42");var subQ2=sQuery(id+"F25.wireOp",EDGE,"E47.rect.right");Q9=makeQuery(id+"F28.boolean.opBoolean","MERGE",EDGE,{"derivedFrom":[makeQuery(id+"F26.boolean.opBoolean","COPY",EDGE,{"disambiguationData":[TD([makeQuery(id+"F22.boolean.opBoolean","COPY",FACE,{"derivedFrom":makeQuery(id+"F22.opExtrude","CAP_FACE",FACE,{"disambiguationData":[OSD([subQ1])],"isStart":false})})])],"derivedFrom":makeQuery(id+"F26.opExtrude","SWEPT_EDGE",EDGE,{"disambiguationData":[OSD([subQ0,subQ2])]})}),makeQuery(id+"F28.opExtrude","SWEPT_EDGE",EDGE,{"disambiguationData":[OSD([sQuery(id+"F27.wireOp",EDGE,"E48.top"),sQuery(id+"F27.wireOp",EDGE,"E48.left")])]})]});}
            var Q10;
            Q10=makeQuery(id+"F28.boolean.opBoolean","COPY",EDGE,{"derivedFrom":makeQuery(id+"F28.opExtrude","SWEPT_EDGE",EDGE,{"disambiguationData":[OSD([sQuery(id+"F25.wireOp",EDGE,"E47.rect.top"),sQuery(id+"F27.wireOp",EDGE,"E48.top"),sQuery(id+"F27.wireOp",EDGE,"E48.right")])]})});
            var Q11;
            Q11=makeQuery(id+"F28.boolean.opBoolean","COPY",EDGE,{"derivedFrom":makeQuery(id+"F28.opExtrude","SWEPT_EDGE",EDGE,{"disambiguationData":[OSD([sQuery(id+"F25.wireOp",EDGE,"E47.rect.bottom"),sQuery(id+"F27.wireOp",EDGE,"E48.bottom"),sQuery(id+"F27.wireOp",EDGE,"E48.right")])]})});
            fillet(context, id + "F29", {"entities" : qUnion([Q0, Q1, Q2, Q3, Q4, Q5, Q6, Q7, Q8, Q9, Q10, Q11]), "radius" : 0.5 * mm, "tangentPropagation" : true, "allowEdgeOverflow" : false});
        }
        {
            var Q0;
            Q0=makeQuery(id+"F1.opExtrude","CAP_EDGE",EDGE,{"disambiguationData":[OSD([sQuery(id+"F0.wireOp",EDGE,"E13.MirrorCS")])],"isStart":false});
            var Q1;
            Q1=makeQuery(id+"F1.opExtrude","CAP_EDGE",EDGE,{"disambiguationData":[OSD([sQuery(id+"F0.wireOp",EDGE,"E13.MirrorCS")])],"isStart":true});
            fillet(context, id + "F30", {"entities" : qUnion([Q0, Q1]), "radius" : 2 * mm, "tangentPropagation" : true, "allowEdgeOverflow" : false});
        }
    });
